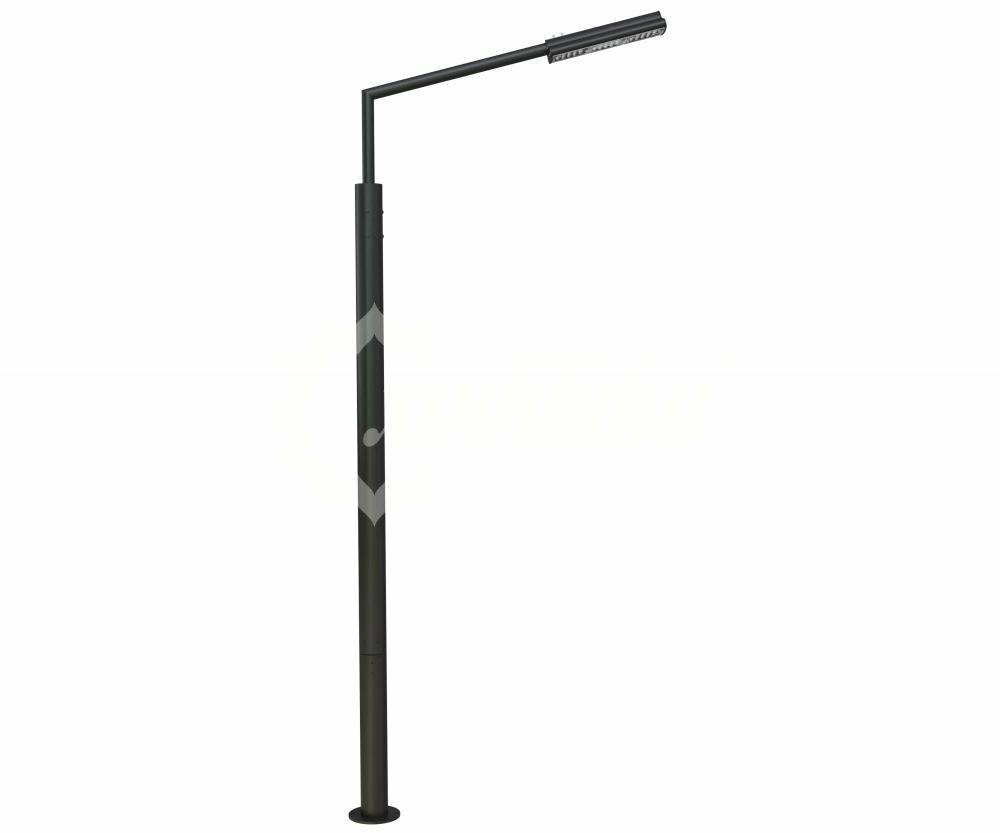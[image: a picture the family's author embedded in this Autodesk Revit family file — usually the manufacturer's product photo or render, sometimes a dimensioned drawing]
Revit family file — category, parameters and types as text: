
# Revit family: 10245 Стальной фонарный столб «Поло-Э» со светильником Хоббика
name_source: partatom
category: Антураж
revit_build: Autodesk Revit 2018 (Build: 20180423_1000(x64)
units: mm (PartAtom-declared; Revit-internal decimal feet)

## family parameters
Всегда вертикально = Да
Источник визуального образа = Геометрия семейства
На основе рабочей плоскости = Нет
Общий = Нет
При загрузке вырезать с полостями = Нет
Точка расчета площади = Нет

## types (4) — shared parameters
URL = https://hobbyka.ru
Артикул товара = Арт. 10245
Группа модели = Светильники со стальными опорами
Изготовитель = ООО «Хоббика»
Изображение типоразмера = Стальной фонарный столб «Поло-Э» со светильником Арт 10245.jpg
Материал изделия = Сталь
Цвет каркаса = Сталь
Ширина = 205 мм

## per-type parameters (varying)
| type | Версия 3,2 м | Версия 4,2 м | Версия 5,2 м | Версия 6,2 м | Высота | Длина | Описание |
| Версия 3,2 м | Да | Нет | Нет | Нет | 3200 мм | 1200 мм | Стальной фонарный столб «Поло-Э» со светильником. Версия 3,2 м |
| Версия 4,2 м | Нет | Да | Нет | Нет | 4200 мм | 1350 мм | Стальной фонарный столб «Поло-Э» со светильником. Версия 4,2 м |
| Версия 5,2 м | Нет | Нет | Да | Нет | 5200 мм | 1350 мм | Стальной фонарный столб «Поло-Э» со светильником. Версия 5,2 м |
| Версия 6,2 м | Нет | Нет | Нет | Да | 6200 мм | 1500 мм | Стальной фонарный столб «Поло-Э» со светильником. Версия 6,2 м |
